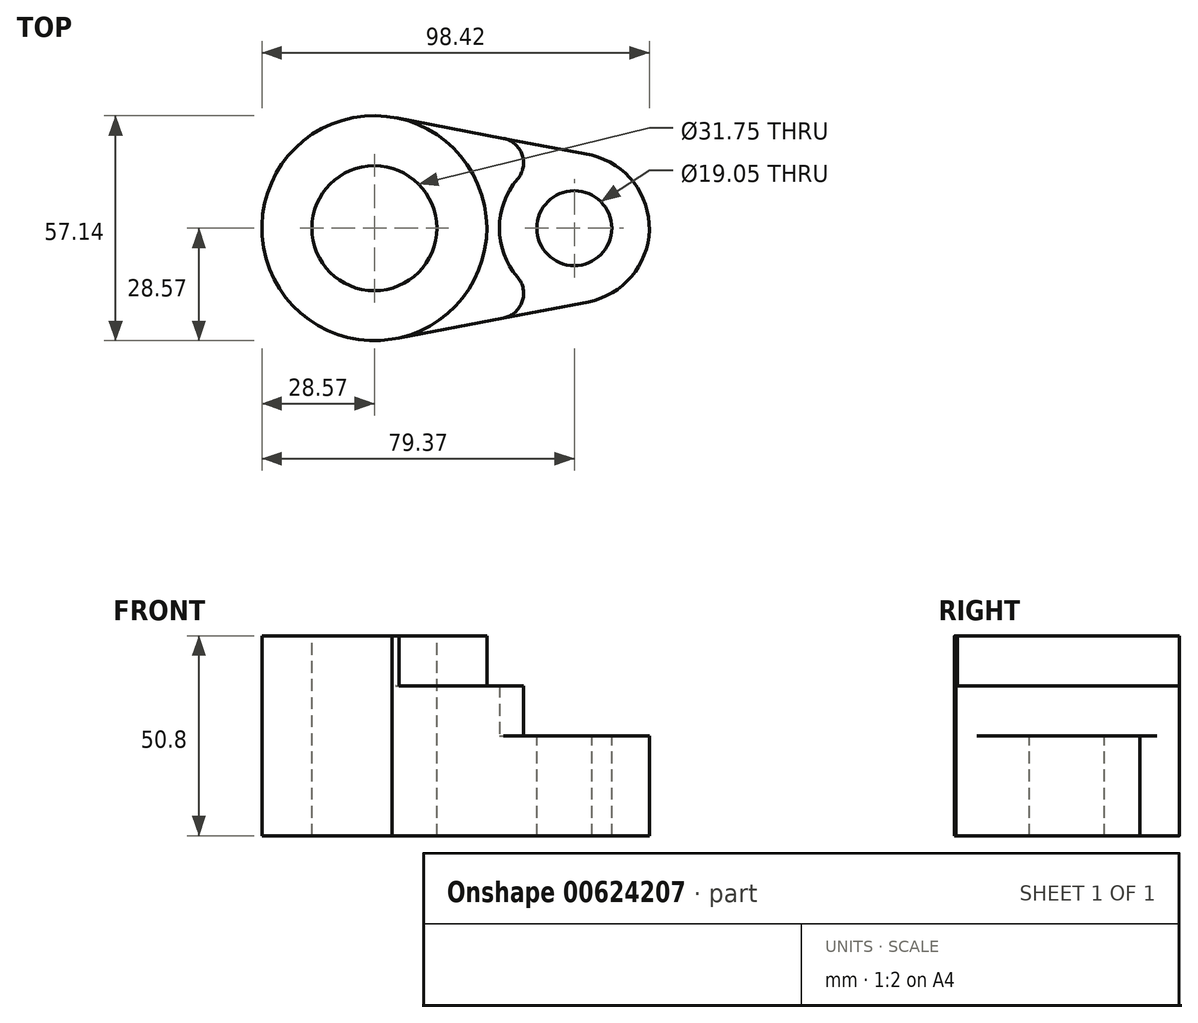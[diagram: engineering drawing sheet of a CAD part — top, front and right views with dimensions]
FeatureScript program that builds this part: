
annotation { "Feature Type Name" : "Feature", "Feature Type Description" : "" }
export const myFeature = defineFeature(function(context is Context, id is Id, definition is map)
    precondition{}
    {
        {
            var Q0;
            Q0=qCreatedBy(makeId("Top.planeOp"),FACE);
            var sketch = newSketch(context, id + "F0", { "sketchPlane" : qUnion([Q0])});
            skCircle(sketch, "E0", {"center": v(0, 0) * mm, "radius": 15.88 * mm});
            skCircle(sketch, "E1", {"center": v(0, 0) * mm, "radius": 28.58 * mm});
            skCircle(sketch, "E2", {"center": v(50.8, 0) * mm, "radius": 9.53 * mm});
            skCircle(sketch, "E3", {"center": v(50.8, 0) * mm, "radius": 19.05 * mm});
            skLineSegment(sketch, "E4", {"start": v(5.37, 28.07) * mm, "end": v(55.26, 18.52) * mm});
            skLineSegment(sketch, "E5", {"start": v(4.46, -28.22) * mm, "end": v(54.37, -18.71) * mm});
            skSolve(sketch);
        }
        {
            var Q0;
            Q0=makeQuery(id+"F0.imprint","IMPRINT",FACE,{"disambiguationData":[TD([[makeQuery(id+"F0.imprint","IMPRINT",EDGE,{"derivedFrom":sQuery(id+"F0.wireOp",EDGE,"E0")}),-1.0]])]});
            var Q1;
            Q1=makeQuery(id+"F0.imprint","IMPRINT",FACE,{"disambiguationData":[TD([[makeQuery(id+"F0.imprint","IMPRINT",EDGE,{"derivedFrom":sQuery(id+"F0.wireOp",EDGE,"E2")}),-1.0]])]});
            var Q2;
            {var subQ0=sQuery(id+"F0.wireOp",EDGE,"E4");var subQ1=sQuery(id+"F0.wireOp",EDGE,"E1");var subQ2=makeQuery(id+"F0.imprint","INTERSECT",VERTEX,{"derivedFrom":[subQ1,subQ0]});Q2=makeQuery(id+"F0.imprint","IMPRINT",FACE,{"disambiguationData":[TD([[makeQuery(id+"F0.imprint","IMPRINT",EDGE,{"disambiguationData":[TD([[subQ2,1.0]])],"derivedFrom":subQ1}),-1.0]])]});}
            extrude(context, id + "F1", {"entities" : qUnion([Q0, Q1, Q2]), "oppositeDirection" : true, "depth" : 25.4 * mm, "offsetDistance" : 25.4 * mm});
        }
        {
            var Q0;
            Q0=makeQuery(id+"F0.imprint","IMPRINT",FACE,{"disambiguationData":[TD([[makeQuery(id+"F0.imprint","IMPRINT",EDGE,{"derivedFrom":sQuery(id+"F0.wireOp",EDGE,"E0")}),-1.0]])]});
            extrude(context, id + "F2", {"entities" : qUnion([Q0]), "operationType" : NewBodyOperationType.ADD, "depth" : 25.4 * mm, "offsetDistance" : 25.4 * mm});
        }
        {
            var Q0;
            {var subQ0=sQuery(id+"F0.wireOp",EDGE,"E4");var subQ1=sQuery(id+"F0.wireOp",EDGE,"E1");var subQ2=makeQuery(id+"F0.imprint","INTERSECT",VERTEX,{"derivedFrom":[subQ1,subQ0]});Q0=makeQuery(id+"F0.imprint","IMPRINT",FACE,{"disambiguationData":[TD([[makeQuery(id+"F0.imprint","IMPRINT",EDGE,{"disambiguationData":[TD([[subQ2,1.0]])],"derivedFrom":subQ1}),-1.0]])]});}
            extrude(context, id + "F3", {"entities" : qUnion([Q0]), "operationType" : NewBodyOperationType.ADD, "depth" : 12.7 * mm, "offsetDistance" : 25.4 * mm});
        }
        {
            var Q0;
            Q0=makeQuery(id+"F3.opExtrude","SWEPT_EDGE",EDGE,{"disambiguationData":[OSD([sQuery(id+"F0.wireOp",EDGE,"E3"),sQuery(id+"F0.wireOp",EDGE,"E5")])]});
            var Q1;
            Q1=makeQuery(id+"F3.opExtrude","SWEPT_EDGE",EDGE,{"disambiguationData":[OSD([sQuery(id+"F0.wireOp",EDGE,"E3"),sQuery(id+"F0.wireOp",EDGE,"E4")])]});
            fillet(context, id + "F4", {"entities" : qUnion([Q0, Q1]), "radius" : 6.35 * mm, "tangentPropagation" : true, "allowEdgeOverflow" : false});
        }
    });
